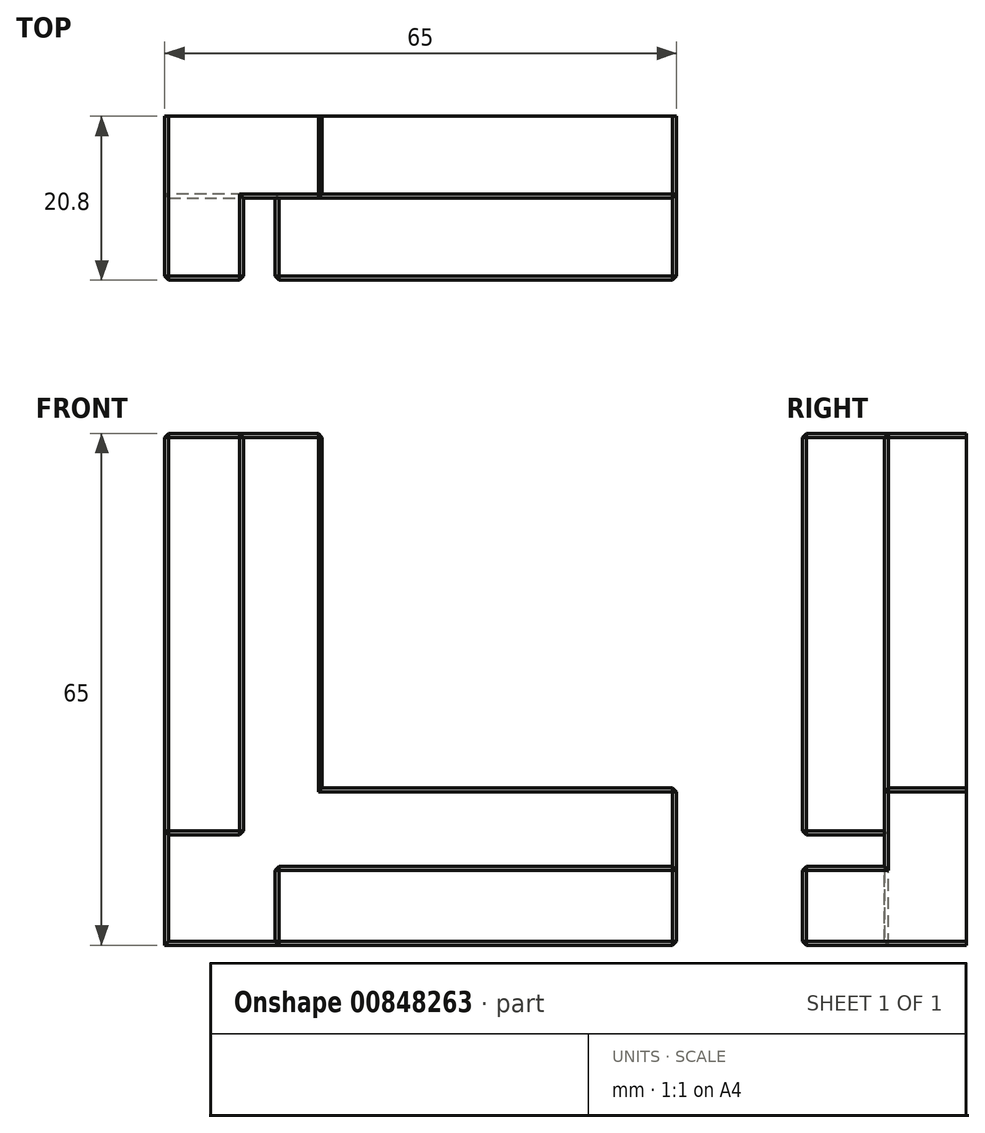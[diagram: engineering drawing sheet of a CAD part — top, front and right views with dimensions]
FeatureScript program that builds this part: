
annotation { "Feature Type Name" : "Feature", "Feature Type Description" : "" }
export const myFeature = defineFeature(function(context is Context, id is Id, definition is map)
    precondition{}
    {
        {
            var Q0;
            Q0=qCreatedBy(makeId("Front.planeOp"),FACE);
            var sketch = newSketch(context, id + "F0", { "sketchPlane" : qUnion([Q0])});
            skLineSegment(sketch, "E0", {"start": v(0, 0) * mm, "end": v(0, 65) * mm});
            skLineSegment(sketch, "E1", {"start": v(0, 65) * mm, "end": v(20, 65) * mm});
            skLineSegment(sketch, "E2", {"start": v(0, 0) * mm, "end": v(65, 0) * mm});
            skLineSegment(sketch, "E3", {"start": v(65, 0) * mm, "end": v(65, 20) * mm});
            skLineSegment(sketch, "E4", {"start": v(20, 65) * mm, "end": v(20, 20) * mm});
            skLineSegment(sketch, "E5", {"start": v(65, 20) * mm, "end": v(20, 20) * mm});
            skSolve(sketch);
        }
        {
            var Q0;
            Q0=makeQuery(id+"F0.imprint","IMPRINT",FACE,{"disambiguationData":[TD([[makeQuery(id+"F0.imprint","IMPRINT",EDGE,{"derivedFrom":sQuery(id+"F0.wireOp",EDGE,"E0")}),-1.0]])]});
            extrude(context, id + "F1", {"entities" : qUnion([Q0]), "depth" : 10.4 * mm, "offsetDistance" : 25 * mm});
        }
        {
            var Q0;
            Q0=makeQuery(id+"F1.opExtrude","CAP_FACE",FACE,{"disambiguationData":[OSD([sQuery(id+"F0.wireOp",EDGE,"E0"),sQuery(id+"F0.wireOp",EDGE,"E1"),sQuery(id+"F0.wireOp",EDGE,"E2"),sQuery(id+"F0.wireOp",EDGE,"E3"),sQuery(id+"F0.wireOp",EDGE,"E4"),sQuery(id+"F0.wireOp",EDGE,"E5")])],"isStart":false});
            var sketch = newSketch(context, id + "F2", { "sketchPlane" : qUnion([Q0])});
            skLineSegment(sketch, "E6.bottom", {"start": v(0, 65) * mm, "end": v(10, 65) * mm});
            skLineSegment(sketch, "E6.top", {"start": v(0, 14) * mm, "end": v(10, 14) * mm});
            skLineSegment(sketch, "E6.left", {"start": v(0, 65) * mm, "end": v(0, 14) * mm});
            skLineSegment(sketch, "E6.right", {"start": v(10, 65) * mm, "end": v(10, 14) * mm});
            skLineSegment(sketch, "E7.bottom", {"start": v(65, 0) * mm, "end": v(14, 0) * mm});
            skLineSegment(sketch, "E7.top", {"start": v(65, 10) * mm, "end": v(14, 10) * mm});
            skLineSegment(sketch, "E7.left", {"start": v(65, 0) * mm, "end": v(65, 10) * mm});
            skLineSegment(sketch, "E7.right", {"start": v(14, 0) * mm, "end": v(14, 10) * mm});
            skSolve(sketch);
        }
        {
            var Q0;
            Q0=makeQuery(id+"F2.imprint","IMPRINT",FACE,{"disambiguationData":[TD([[makeQuery(id+"F2.imprint","IMPRINT",EDGE,{"derivedFrom":sQuery(id+"F2.wireOp",EDGE,"E6.bottom")}),-1.0]])]});
            var Q1;
            Q1=makeQuery(id+"F2.imprint","IMPRINT",FACE,{"disambiguationData":[TD([[makeQuery(id+"F2.imprint","IMPRINT",EDGE,{"derivedFrom":sQuery(id+"F2.wireOp",EDGE,"E7.bottom")}),1.0]])]});
            extrude(context, id + "F3", {"entities" : qUnion([Q0, Q1]), "operationType" : NewBodyOperationType.ADD, "depth" : 10.4 * mm, "offsetDistance" : 25 * mm});
        }
        {
            var Q0;
            Q0=makeQuery(id+"F1.opExtrude","CAP_EDGE",EDGE,{"disambiguationData":[OSD([sQuery(id+"F0.wireOp",EDGE,"E4")])],"isStart":false});
            var Q1;
            Q1=makeQuery(id+"F1.opExtrude","CAP_EDGE",EDGE,{"disambiguationData":[OSD([sQuery(id+"F0.wireOp",EDGE,"E1")])],"isStart":false});
            var Q2;
            Q2=makeQuery(id+"F3.opExtrude","CAP_EDGE",EDGE,{"disambiguationData":[OSD([sQuery(id+"F2.wireOp",EDGE,"E6.bottom")])],"isStart":false});
            var Q3;
            Q3=makeQuery(id+"F3.opExtrude","CAP_FACE",FACE,{"disambiguationData":[OSD([sQuery(id+"F2.wireOp",EDGE,"E6.bottom"),sQuery(id+"F2.wireOp",EDGE,"E6.top"),sQuery(id+"F2.wireOp",EDGE,"E6.left"),sQuery(id+"F2.wireOp",EDGE,"E6.right")])],"isStart":false});
            var Q4;
            Q4=makeQuery(id+"F3.opExtrude","CAP_FACE",FACE,{"disambiguationData":[OSD([sQuery(id+"F2.wireOp",EDGE,"E7.bottom"),sQuery(id+"F2.wireOp",EDGE,"E7.top"),sQuery(id+"F2.wireOp",EDGE,"E7.left"),sQuery(id+"F2.wireOp",EDGE,"E7.right")])],"isStart":false});
            var Q5;
            Q5=makeQuery(id+"F1.opExtrude","CAP_EDGE",EDGE,{"disambiguationData":[OSD([sQuery(id+"F0.wireOp",EDGE,"E3")])],"isStart":false});
            var Q6;
            Q6=makeQuery(id+"F3.opExtrude","SWEPT_EDGE",EDGE,{"disambiguationData":[OSD([sQuery(id+"F0.wireOp",EDGE,"E3"),sQuery(id+"F2.wireOp",EDGE,"E7.top"),sQuery(id+"F2.wireOp",EDGE,"E7.left")])]});
            var Q7;
            Q7=makeQuery(id+"F3.opExtrude","SWEPT_EDGE",EDGE,{"disambiguationData":[OSD([sQuery(id+"F0.wireOp",EDGE,"E1"),sQuery(id+"F2.wireOp",EDGE,"E6.bottom"),sQuery(id+"F2.wireOp",EDGE,"E6.right")])]});
            var Q8;
            Q8=makeQuery(id+"F1.opExtrude","SWEPT_EDGE",EDGE,{"disambiguationData":[OSD([sQuery(id+"F0.wireOp",EDGE,"E1"),sQuery(id+"F0.wireOp",EDGE,"E4")])]});
            var Q9;
            Q9=makeQuery(id+"F1.opExtrude","SWEPT_EDGE",EDGE,{"disambiguationData":[OSD([sQuery(id+"F0.wireOp",EDGE,"E3"),sQuery(id+"F0.wireOp",EDGE,"E5")])]});
            var Q10;
            Q10=makeQuery(id+"F1.opExtrude","CAP_EDGE",EDGE,{"disambiguationData":[OSD([sQuery(id+"F0.wireOp",EDGE,"E5")])],"isStart":false});
            var Q11;
            Q11=makeQuery(id+"F1.opExtrude","CAP_EDGE",EDGE,{"disambiguationData":[OSD([sQuery(id+"F0.wireOp",EDGE,"E0")])],"isStart":false});
            var Q12;
            Q12=makeQuery(id+"F1.opExtrude","CAP_EDGE",EDGE,{"disambiguationData":[OSD([sQuery(id+"F0.wireOp",EDGE,"E2")])],"isStart":false});
            var Q13;
            Q13=makeQuery(id+"F3.opExtrude","SWEPT_EDGE",EDGE,{"disambiguationData":[OSD([sQuery(id+"F0.wireOp",EDGE,"E2"),sQuery(id+"F2.wireOp",EDGE,"E7.bottom"),sQuery(id+"F2.wireOp",EDGE,"E7.right")])]});
            var Q14;
            Q14=makeQuery(id+"F3.opExtrude","SWEPT_EDGE",EDGE,{"disambiguationData":[OSD([sQuery(id+"F0.wireOp",EDGE,"E0"),sQuery(id+"F2.wireOp",EDGE,"E6.top"),sQuery(id+"F2.wireOp",EDGE,"E6.left")])]});
            var Q15;
            Q15=makeQuery(id+"F3.opExtrude","SWEPT_EDGE",EDGE,{"disambiguationData":[OSD([sQuery(id+"F2.wireOp",EDGE,"E6.top"),sQuery(id+"F2.wireOp",EDGE,"E6.right")])]});
            var Q16;
            Q16=makeQuery(id+"F3.opExtrude","SWEPT_EDGE",EDGE,{"disambiguationData":[OSD([sQuery(id+"F2.wireOp",EDGE,"E7.top"),sQuery(id+"F2.wireOp",EDGE,"E7.right")])]});
            var Q17;
            Q17=makeQuery(id+"F3.boolean.opBoolean","MERGE",EDGE,{"derivedFrom":[makeQuery(id+"F1.opExtrude","SWEPT_EDGE",EDGE,{"disambiguationData":[OSD([sQuery(id+"F0.wireOp",EDGE,"E0"),sQuery(id+"F0.wireOp",EDGE,"E1")])]}),makeQuery(id+"F3.opExtrude","SWEPT_EDGE",EDGE,{"disambiguationData":[OSD([sQuery(id+"F2.wireOp",EDGE,"E6.bottom"),sQuery(id+"F2.wireOp",EDGE,"E6.left")])]})]});
            var Q18;
            Q18=makeQuery(id+"F3.boolean.opBoolean","MERGE",EDGE,{"derivedFrom":[makeQuery(id+"F1.opExtrude","SWEPT_EDGE",EDGE,{"disambiguationData":[OSD([sQuery(id+"F0.wireOp",EDGE,"E2"),sQuery(id+"F0.wireOp",EDGE,"E3")])]}),makeQuery(id+"F3.opExtrude","SWEPT_EDGE",EDGE,{"disambiguationData":[OSD([sQuery(id+"F2.wireOp",EDGE,"E7.bottom"),sQuery(id+"F2.wireOp",EDGE,"E7.left")])]})]});
            chamfer(context, id + "F4", {"entities" : qUnion([Q0, Q1, Q2, Q3, Q4, Q5, Q6, Q7, Q8, Q9, Q10, Q11, Q12, Q13, Q14, Q15, Q16, Q17, Q18]), "width" : 0.5 * mm, "tangentPropagation" : true});
        }
    });
